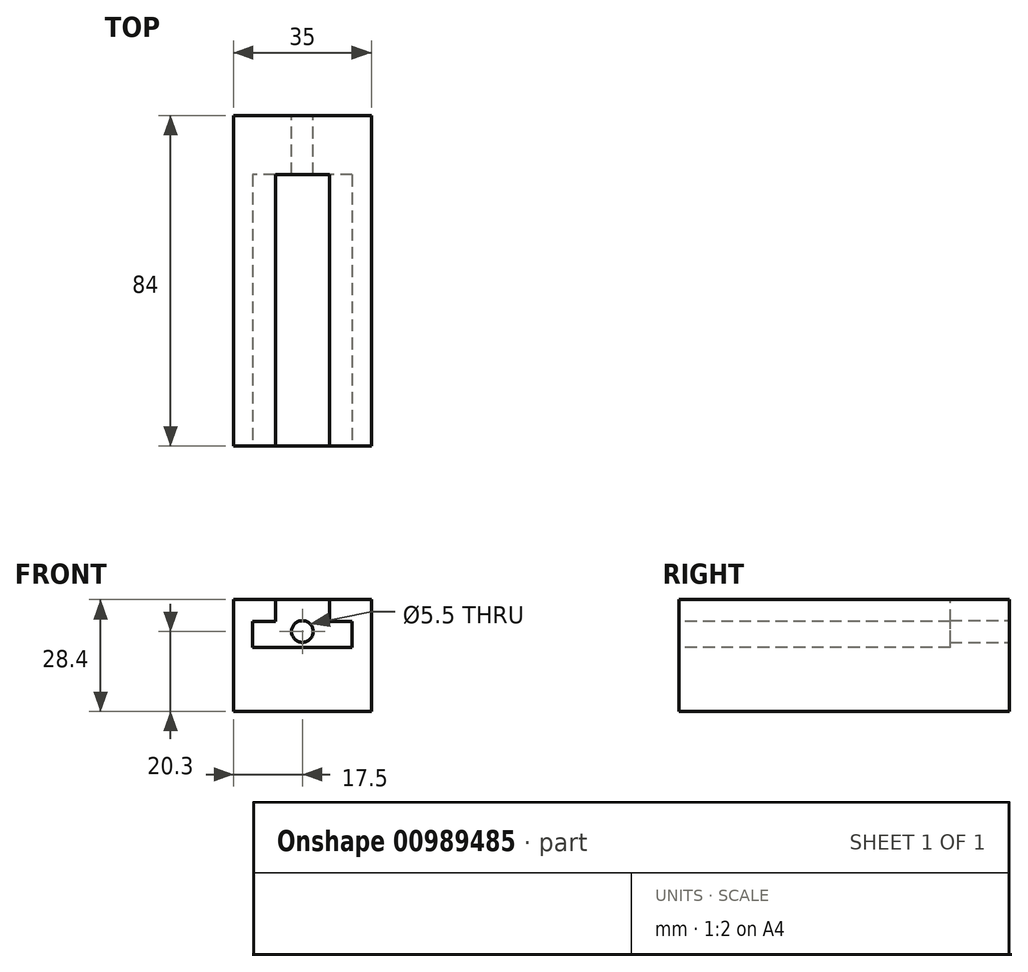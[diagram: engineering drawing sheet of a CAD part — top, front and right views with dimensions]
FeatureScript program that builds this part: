
annotation { "Feature Type Name" : "Feature", "Feature Type Description" : "" }
export const myFeature = defineFeature(function(context is Context, id is Id, definition is map)
    precondition{}
    {
        {
            var Q0;
            Q0=qCreatedBy(makeId("Front.planeOp"),FACE);
            var sketch = newSketch(context, id + "F0", { "sketchPlane" : qUnion([Q0])});
            skLineSegment(sketch, "E0.bottom", {"start": v(-17.5, -19.6) * mm, "end": v(17.5, -19.6) * mm});
            skLineSegment(sketch, "E0.top", {"start": v(-17.5, 19.6) * mm, "end": v(17.5, 19.6) * mm});
            skLineSegment(sketch, "E0.left", {"start": v(-17.5, -19.6) * mm, "end": v(-17.5, 19.6) * mm});
            skLineSegment(sketch, "E0.right", {"start": v(17.5, -19.6) * mm, "end": v(17.5, 19.6) * mm});
            skPoint(sketch, "E0.middle", {"position": v(0, 0) * mm});
            skSolve(sketch);
        }
        {
            var Q0;
            Q0 = qSketchRegion(id + "F0", true);
            extrude(context, id + "F1", {"entities" : qUnion([Q0]), "depth" : 84 * mm, "offsetDistance" : 25.4 * mm});
        }
        {
            var Q0;
            Q0=makeQuery(id+"F1.opExtrude","CAP_FACE",FACE,{"disambiguationData":[OSD([sQuery(id+"F0.wireOp",EDGE,"E0.bottom"),sQuery(id+"F0.wireOp",EDGE,"E0.top"),sQuery(id+"F0.wireOp",EDGE,"E0.left"),sQuery(id+"F0.wireOp",EDGE,"E0.right")])],"isStart":false});
            var sketch = newSketch(context, id + "F2", { "sketchPlane" : qUnion([Q0])});
            skLineSegment(sketch, "E1.bottom", {"start": v(12.62, 3.3) * mm, "end": v(6.87, 3.3) * mm});
            skLineSegment(sketch, "E1.top", {"start": v(12.62, -3.3) * mm, "end": v(-12.62, -3.3) * mm});
            skLineSegment(sketch, "E1.left", {"start": v(12.62, -3.3) * mm, "end": v(12.62, 3.3) * mm});
            skLineSegment(sketch, "E1.right", {"start": v(-12.62, -3.3) * mm, "end": v(-12.62, 3.3) * mm});
            skPoint(sketch, "E1.middle", {"position": v(0, 0) * mm});
            skLineSegment(sketch, "E2.left", {"start": v(6.87, 3.3) * mm, "end": v(6.87, 8.8) * mm});
            skLineSegment(sketch, "E2.right", {"start": v(-6.87, 3.3) * mm, "end": v(-6.87, 8.8) * mm});
            skPoint(sketch, "E2.middle", {"position": v(0, 19.6) * mm});
            skLineSegment(sketch, "E3.trimOffspring", {"start": v(-6.87, 3.3) * mm, "end": v(-12.62, 3.3) * mm});
            skLineSegment(sketch, "E4", {"start": v(-6.87, 8.8) * mm, "end": v(6.87, 8.8) * mm});
            skSolve(sketch);
        }
        {
            var Q0;
            Q0 = qSketchRegion(id + "F2", true);
            extrude(context, id + "F3", {"entities" : qUnion([Q0]), "operationType" : NewBodyOperationType.REMOVE, "oppositeDirection" : true, "depth" : 69 * mm, "offsetDistance" : 25.4 * mm});
        }
        {
            var Q0;
            Q0=makeQuery(id+"F1.opExtrude","CAP_FACE",FACE,{"disambiguationData":[OSD([sQuery(id+"F0.wireOp",EDGE,"E0.bottom"),sQuery(id+"F0.wireOp",EDGE,"E0.top"),sQuery(id+"F0.wireOp",EDGE,"E0.left"),sQuery(id+"F0.wireOp",EDGE,"E0.right")])],"isStart":true});
            var sketch = newSketch(context, id + "F4", { "sketchPlane" : qUnion([Q0])});
            skPoint(sketch, "E5", {"position": v(0, 0.7) * mm});
            skSolve(sketch);
        }
        {
            var Q0;
            Q0=sQuery(id+"F4.wireOp",VERTEX,"E5");
            var Q1;
            Q1=makeQuery(id+"F1.opExtrude","SWEPT_BODY",BODY,{"disambiguationData":[OSD([sQuery(id+"F0.wireOp",EDGE,"E0.bottom"),sQuery(id+"F0.wireOp",EDGE,"E0.top"),sQuery(id+"F0.wireOp",EDGE,"E0.left"),sQuery(id+"F0.wireOp",EDGE,"E0.right")])]});
            hole(context, id + "F5", {"style" : HoleStyle.SIMPLE, "endStyle" : HoleEndStyle.THROUGH, "standardTappedOrClearance" : lookupTablePath({ "fit" : "Normal", "standard" : "ISO", "size" : "M5", "type" : "Clearance" }), "standardBlindInLast" : lookupTablePath({ "fit" : "Normal", "standard" : "ISO", "engagement" : "75%", "pitch" : "0.8 mm", "size" : "M5", "type" : "Clearance & tapped" }), "holeDiameter" : 5.5 * mm, "majorDiameter" : 6.35 * mm, "isTappedThrough" : true, "tappedDepth" : 12.7 * mm, "tapClearance" : 3, "locations" : qUnion([Q0]), "scope" : qUnion([Q1])});
        }
        {
            var Q0;
            Q0=makeQuery(id+"F1.opExtrude","CAP_FACE",FACE,{"disambiguationData":[OSD([sQuery(id+"F0.wireOp",EDGE,"E0.bottom"),sQuery(id+"F0.wireOp",EDGE,"E0.top"),sQuery(id+"F0.wireOp",EDGE,"E0.left"),sQuery(id+"F0.wireOp",EDGE,"E0.right")])],"isStart":false});
            var sketch = newSketch(context, id + "F6", { "sketchPlane" : qUnion([Q0])});
            skLineSegment(sketch, "E6.bottom", {"start": v(-17.5, 19.6) * mm, "end": v(17.5, 19.6) * mm});
            skLineSegment(sketch, "E6.top", {"start": v(-17.5, 8.8) * mm, "end": v(17.5, 8.8) * mm});
            skLineSegment(sketch, "E6.left", {"start": v(-17.5, 19.6) * mm, "end": v(-17.5, 8.8) * mm});
            skLineSegment(sketch, "E6.right", {"start": v(17.5, 19.6) * mm, "end": v(17.5, 8.8) * mm});
            skSolve(sketch);
        }
        {
            var Q0;
            Q0 = qSketchRegion(id + "F6", true);
            extrude(context, id + "F7", {"entities" : qUnion([Q0]), "operationType" : NewBodyOperationType.REMOVE, "endBound" : BoundingType.THROUGH_ALL, "oppositeDirection" : true, "depth" : 25 * mm, "offsetDistance" : 25 * mm});
        }
    });
